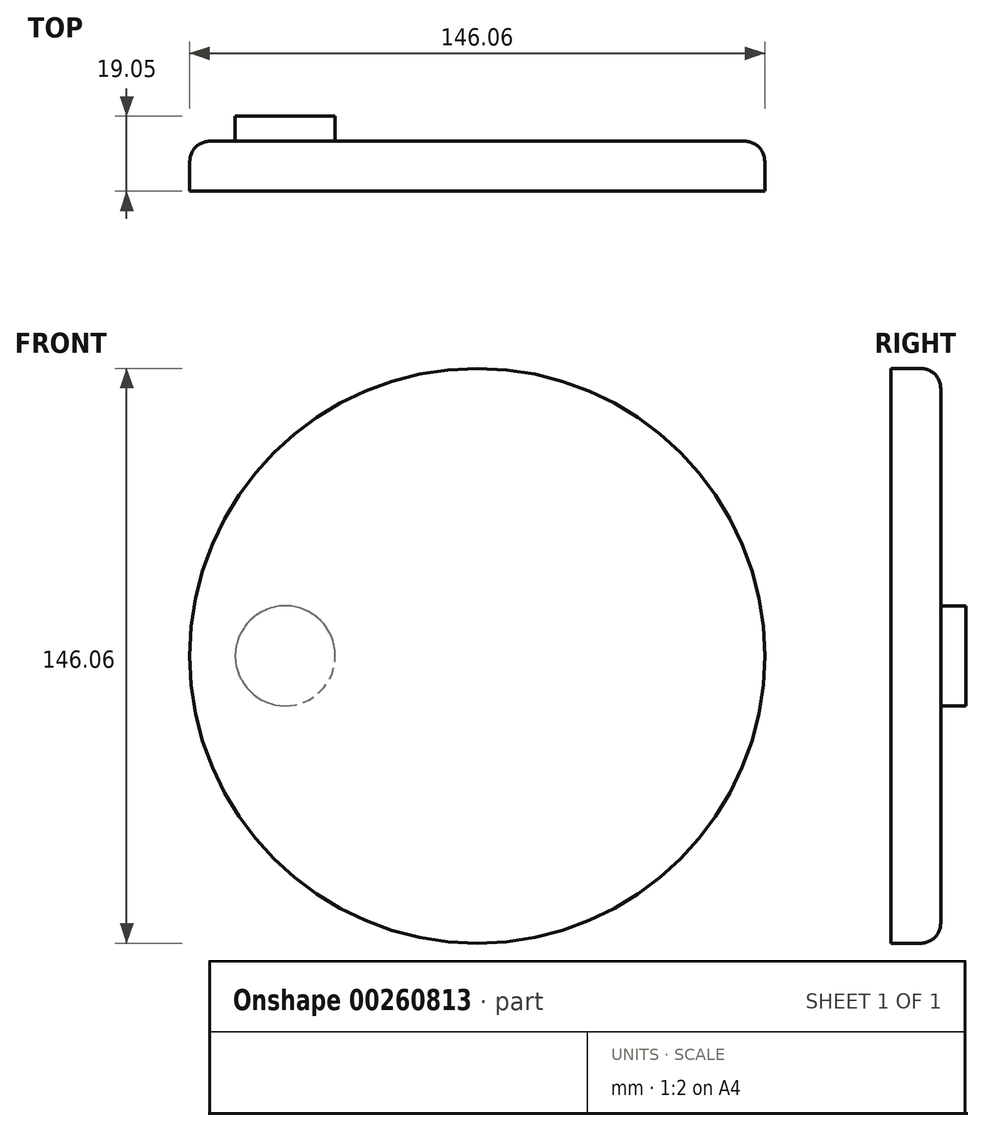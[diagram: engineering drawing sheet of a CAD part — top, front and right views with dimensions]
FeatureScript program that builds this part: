
annotation { "Feature Type Name" : "Feature", "Feature Type Description" : "" }
export const myFeature = defineFeature(function(context is Context, id is Id, definition is map)
    precondition{}
    {
        {
            var Q0;
            Q0=qCreatedBy(makeId("Front.planeOp"),FACE);
            var sketch = newSketch(context, id + "F0", { "sketchPlane" : qUnion([Q0])});
            skCircle(sketch, "E0", {"center": v(0, 0) * mm, "radius": 73.03 * mm});
            skSolve(sketch);
        }
        {
            var Q0;
            Q0=makeQuery(id+"F0.imprint","IMPRINT",FACE,{"disambiguationData":[TD([[makeQuery(id+"F0.imprint","IMPRINT",EDGE,{"derivedFrom":sQuery(id+"F0.wireOp",EDGE,"E0")}),1.0]])]});
            extrude(context, id + "F1", {"entities" : qUnion([Q0]), "oppositeDirection" : true, "depth" : 12.7 * mm});
        }
        {
            var Q0;
            Q0=makeQuery(id+"F1.opExtrude","CAP_EDGE",EDGE,{"disambiguationData":[OSD([sQuery(id+"F0.wireOp",EDGE,"E0")])],"isStart":false});
            fillet(context, id + "F2", {"entities" : qUnion([Q0]), "radius" : 5.08 * mm, "tangentPropagation" : true, "allowEdgeOverflow" : false});
        }
        {
            var Q0;
            Q0=makeQuery(id+"F1.opExtrude","CAP_FACE",FACE,{"disambiguationData":[OSD([sQuery(id+"F0.wireOp",EDGE,"E0")])],"isStart":false});
            var sketch = newSketch(context, id + "F3", { "sketchPlane" : qUnion([Q0])});
            skCircle(sketch, "E1", {"center": v(48.77, 0) * mm, "radius": 12.7 * mm});
            skSolve(sketch);
        }
        {
            var Q0;
            Q0=makeQuery(id+"F3.imprint","IMPRINT",FACE,{"disambiguationData":[TD([[makeQuery(id+"F3.imprint","IMPRINT",EDGE,{"derivedFrom":sQuery(id+"F3.wireOp",EDGE,"E1")}),1.0]])]});
            extrude(context, id + "F4", {"entities" : qUnion([Q0]), "operationType" : NewBodyOperationType.ADD, "depth" : 6.35 * mm});
        }
    });
